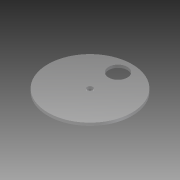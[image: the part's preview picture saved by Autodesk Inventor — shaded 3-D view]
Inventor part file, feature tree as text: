
AUTODESK INVENTOR PART (.ipt)
format: ipt  version: 2015 (Build 190159000, 159)  size: 79,360 bytes
history: native  units: mm
features: extrude x1, sketch x1
ambient origin geometry x8: Origin, YZ Plane, XZ Plane, XY Plane, X Axis, Y Axis, Z Axis, Center Point
bodies: Body1 (feature_tree)
feature tree (2):
  extrude  "Extrusion2"  Depth=3.0mm
  sketch  "Sketch1"  dims[d0=90.0mm d1=5.9mm d4=20.0mm d6=30.0mm d7=3.0mm d8=0.0mm]
